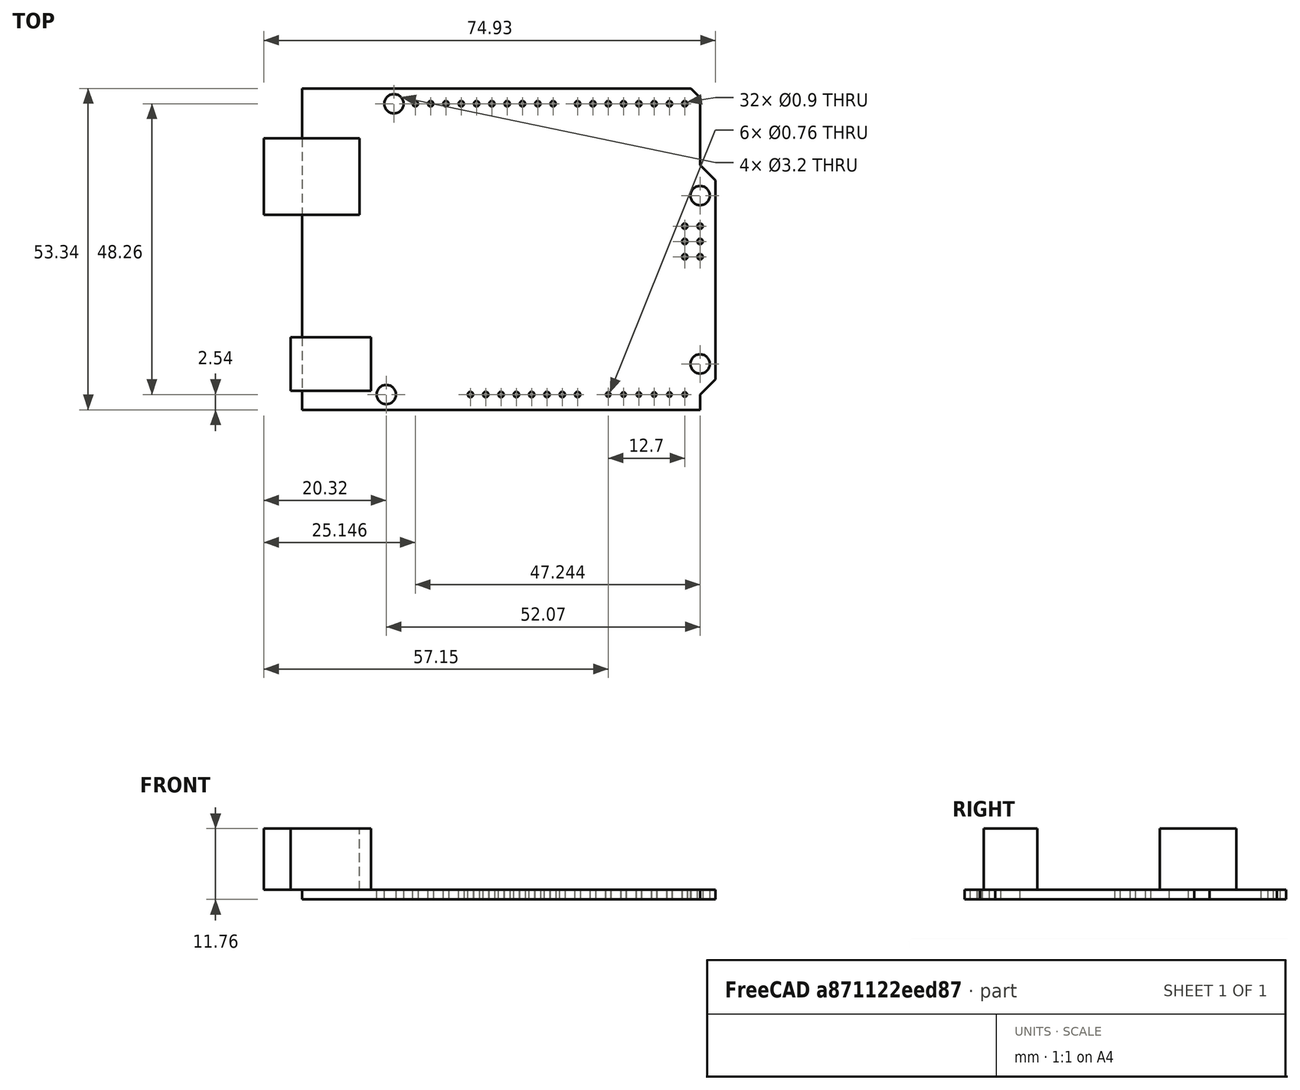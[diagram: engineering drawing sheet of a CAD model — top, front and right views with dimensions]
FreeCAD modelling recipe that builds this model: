
FCSTD DOCUMENT  (FreeCAD 0.21R33694 (Git))
Label: 2405_ARDUNIV
License: All rights reserved
LicenseURL: http://en.wikipedia.org/wiki/All_rights_reserved
objects: TechDraw::DrawViewDimension×40, Sketcher::SketchObject×8, PartDesign::Pocket×6, PartDesign::Pad×2, PartDesign::Body×1, TechDraw::DrawSVGTemplate×1, TechDraw::DrawViewPart×1, TechDraw::DrawPage×1
note: 103 computed .brp shape members not serialized (recipe doc carries the construction recipe); baked Part::Feature solids carry a one-line shape summary decoded from their .brp

FEATURE [Sketcher::SketchObject] Sketch
  FullyConstrained = true
  MapMode = 5
  Support = -> [XY_Plane]
  sketch-geometry (9):
    g0: LineSegment StartX=0 StartY=0 StartZ=0 EndX=66.04 EndY=0 EndZ=0
    g1: LineSegment StartX=66.04 StartY=0 StartZ=0 EndX=66.04 EndY=2.54 EndZ=0
    g2: LineSegment StartX=64.516 StartY=53.34 StartZ=0 EndX=0 EndY=53.34 EndZ=0
    g3: LineSegment StartX=0 StartY=53.34 StartZ=0 EndX=0 EndY=0 EndZ=0
    g4: LineSegment StartX=64.516 StartY=53.34 StartZ=0 EndX=66.04 EndY=51.816 EndZ=0
    g5: LineSegment StartX=66.04 StartY=40.64 StartZ=0 EndX=68.58 EndY=38.1 EndZ=0
    g6: LineSegment StartX=68.58 StartY=38.1 StartZ=0 EndX=68.58 EndY=5.08 EndZ=0
    g7: LineSegment StartX=68.58 StartY=5.08 StartZ=0 EndX=66.04 EndY=2.54 EndZ=0
    g8: LineSegment StartX=66.04 StartY=40.64 StartZ=0 EndX=66.04 EndY=51.816 EndZ=0
  constraints (26):
    c: Coincident(g0,g1)
    c: Coincident(g2,g3)
    c: Coincident(g3,g0)
    c: Horizontal(g0)
    c: Horizontal(g2)
    c: Vertical(g1)
    c: Vertical(g3)
    c: Coincident(g0,g-1)
    c: DistanceY(g3,g3) = 53.34
    c: Coincident(g5,g6)
    c: Vertical(g6)
    c: Coincident(g6,g7)
    c: Coincident(g2,g4)
    c: Coincident(g4,g8)
    c: Coincident(g8,g5)
    c: Coincident(g7,g1)
    c: DistanceY(g1,g1) = 2.54
    c: Distance(g6,g-1) = 5.08
    c: Distance(g6,g1) = 2.54
    c: DistanceX(g2,g2) = 64.516
    c: Distance(g4,g-1) = 51.816
    c: Vertical(g5,g1)
    c: Vertical(g8)
    c: Distance(g5,g-1) = 40.64
    c: Distance(g5,g-1) = 38.1
    c: Distance(g6,g3) = 68.58
FEATURE [PartDesign::Pad] Pad
  Direction = (0,0,1)
  Length = 1.6
  Length2 = 10
  Profile = -> Sketch
  ReferenceAxis = -> Sketch [N_Axis]
  Reversed = true
  Type = 0
FEATURE [Sketcher::SketchObject] Sketch001
  FullyConstrained = true
  MapMode = 5
  Support = -> [XY_Plane]
  sketch-geometry (8):
    g0: LineSegment StartX=-1.905 StartY=12.065 StartZ=0 EndX=11.43 EndY=12.065 EndZ=0
    g1: LineSegment StartX=11.43 StartY=12.065 StartZ=0 EndX=11.43 EndY=3.175 EndZ=0
    g2: LineSegment StartX=11.43 StartY=3.175 StartZ=0 EndX=-1.905 EndY=3.175 EndZ=0
    g3: LineSegment StartX=-1.905 StartY=3.175 StartZ=0 EndX=-1.905 EndY=12.065 EndZ=0
    g4: LineSegment StartX=-6.35 StartY=45.085 StartZ=0 EndX=9.525 EndY=45.085 EndZ=0
    g5: LineSegment StartX=9.525 StartY=45.085 StartZ=0 EndX=9.525 EndY=32.385 EndZ=0
    g6: LineSegment StartX=9.525 StartY=32.385 StartZ=0 EndX=-6.35 EndY=32.385 EndZ=0
    g7: LineSegment StartX=-6.35 StartY=32.385 StartZ=0 EndX=-6.35 EndY=45.085 EndZ=0
  constraints (24):
    c: Coincident(g0,g1)
    c: Coincident(g1,g2)
    c: Coincident(g2,g3)
    c: Coincident(g3,g0)
    c: Horizontal(g0)
    c: Horizontal(g2)
    c: Vertical(g1)
    c: Vertical(g3)
    c: Coincident(g4,g5)
    c: Coincident(g5,g6)
    c: Coincident(g6,g7)
    c: Coincident(g7,g4)
    c: Horizontal(g4)
    c: Horizontal(g6)
    c: Vertical(g5)
    c: Vertical(g7)
    c: Distance(g2,g-2) = 1.905
    c: Distance(g2,g-1) = 3.175
    c: DistanceY(g3,g3) = 8.89
    c: DistanceX(g0,g0) = 13.335
    c: Distance(g4,g-2) = 6.35
    c: Distance(g6,g-1) = 32.385
    c: DistanceY(g7,g7) = 12.7
    c: DistanceX(g4,g4) = 15.875
FEATURE [PartDesign::Pad] Pad001
  BaseFeature = -> Pad
  Direction = (0,0,1)
  Length = 10.16
  Length2 = 10
  Profile = -> Sketch001
  ReferenceAxis = -> Sketch001 [N_Axis]
  Type = 0
FEATURE [Sketcher::SketchObject] Sketch002
  FullyConstrained = true
  MapMode = 5
  Support = -> [XY_Plane]
  sketch-geometry (4):
    g0: Circle CenterX=13.97 CenterY=2.54 CenterZ=0 NormalX=0 NormalY=0 NormalZ=1 AngleXU=0 Radius=1.6
    g1: Circle CenterX=15.24 CenterY=50.8 CenterZ=0 NormalX=0 NormalY=0 NormalZ=1 AngleXU=0 Radius=1.6
    g2: Circle CenterX=66.04 CenterY=35.56 CenterZ=0 NormalX=0 NormalY=0 NormalZ=1 AngleXU=0 Radius=1.6
    g3: Circle CenterX=66.04 CenterY=7.62 CenterZ=0 NormalX=0 NormalY=0 NormalZ=1 AngleXU=0 Radius=1.6
  constraints (12):
    c: Equal(g1,g2)
    c: Equal(g2,g3)
    c: Equal(g3,g0)
    c: Radius(g1) = 1.6
    c: Distance(g0,g-1) = 2.54
    c: Distance(g0,g-2) = 13.97
    c: Distance(g1,g-1) = 50.8
    c: Distance(g1,g-2) = 15.24
    c: Distance(g3,g-1) = 7.62
    c: Distance(g3,g-2) = 66.04
    c: Vertical(g2,g3)
    c: Distance(g2,g-1) = 35.56
FEATURE [PartDesign::Pocket] Pocket
  BaseFeature = -> Pad001
  Direction = (0,0,-1)
  Length = 5.00126
  Length2 = 5
  Profile = -> Sketch002
  ReferenceAxis = -> Sketch002 [N_Axis]
  Type = 0
FEATURE [Sketcher::SketchObject] Sketch003
  FullyConstrained = true
  MapMode = 5
  Support = -> [XY_Plane]
  sketch-geometry (6):
    g0: Circle CenterX=63.5 CenterY=30.48 CenterZ=0 NormalX=0 NormalY=0 NormalZ=1 AngleXU=0 Radius=0.45
    g1: Circle CenterX=63.5 CenterY=27.94 CenterZ=0 NormalX=0 NormalY=0 NormalZ=1 AngleXU=0 Radius=0.45
    g2: Circle CenterX=63.5 CenterY=25.4 CenterZ=0 NormalX=0 NormalY=0 NormalZ=1 AngleXU=0 Radius=0.45
    g3: Circle CenterX=66.04 CenterY=30.48 CenterZ=0 NormalX=0 NormalY=0 NormalZ=1 AngleXU=0 Radius=0.45
    g4: Circle CenterX=66.04 CenterY=27.94 CenterZ=0 NormalX=0 NormalY=0 NormalZ=1 AngleXU=0 Radius=0.45
    g5: Circle CenterX=66.04 CenterY=25.4 CenterZ=0 NormalX=0 NormalY=0 NormalZ=1 AngleXU=0 Radius=0.45
  constraints (18):
    c: Distance(g0,g-2) = 63.5
    c: Distance(g0,g-1) = 30.48
    c: Radius(g0) = 0.45
    c: Equal(g1,g0)
    c: Equal(g0,g3)
    c: Equal(g3,g4)
    c: Equal(g4,g5)
    c: Equal(g5,g2)
    c: Vertical(g0,g1)
    c: Vertical(g1,g2)
    c: Vertical(g3,g4)
    c: Vertical(g4,g5)
    c: Horizontal(g0,g3)
    c: Horizontal(g4,g1)
    c: Horizontal(g5,g2)
    c: Distance(g0,g1) = 2.54
    c: Distance(g1,g2) = 2.54
    c: Distance(g2,g5) = 2.54
FEATURE [PartDesign::Pocket] Pocket001
  BaseFeature = -> Pocket
  Direction = (0,0,-1)
  Length = 5.00126
  Length2 = 5
  Profile = -> Sketch003
  ReferenceAxis = -> Sketch003 [N_Axis]
  Type = 0
FEATURE [Sketcher::SketchObject] Sketch004
  FullyConstrained = true
  MapMode = 5
  Support = -> [XY_Plane]
  sketch-geometry (9):
    g0: Circle CenterX=27.94 CenterY=2.54 CenterZ=0 NormalX=0 NormalY=0 NormalZ=1 AngleXU=0 Radius=0.45
    g1: Circle CenterX=30.48 CenterY=2.54 CenterZ=0 NormalX=0 NormalY=0 NormalZ=1 AngleXU=0 Radius=0.45
    g2: Circle CenterX=33.02 CenterY=2.54 CenterZ=0 NormalX=0 NormalY=0 NormalZ=1 AngleXU=0 Radius=0.45
    g3: Circle CenterX=35.56 CenterY=2.54 CenterZ=0 NormalX=0 NormalY=0 NormalZ=1 AngleXU=0 Radius=0.45
    g4: Circle CenterX=40.64 CenterY=2.54 CenterZ=0 NormalX=0 NormalY=0 NormalZ=1 AngleXU=0 Radius=0.45
    g5: Circle CenterX=43.18 CenterY=2.54 CenterZ=0 NormalX=0 NormalY=0 NormalZ=1 AngleXU=0 Radius=0.45
    g6: Circle CenterX=45.72 CenterY=2.54 CenterZ=0 NormalX=0 NormalY=0 NormalZ=1 AngleXU=0 Radius=0.45
    g7: LineSegment StartX=27.94 StartY=2.54 StartZ=0 EndX=45.72 EndY=2.54 EndZ=0
    g8: Circle CenterX=38.1 CenterY=2.54 CenterZ=0 NormalX=0 NormalY=0 NormalZ=1 AngleXU=0 Radius=0.45
  constraints (26):
    c: Equal(g0,g1)
    c: Equal(g1,g2)
    c: Equal(g2,g3)
    c: Equal(g3,g4)
    c: Equal(g4,g5)
    c: Radius(g0) = 0.45
    c: Distance(g0,g-2) = 27.94
    c: Distance(g0,g-1) = 2.54
    c: Coincident(g7,g0)
    c: Coincident(g7,g6)
    c: Horizontal(g7)
    c: DistanceX(g7,g7) = 17.78
    c: PointOnObject(g1,g7)
    c: PointOnObject(g2,g7)
    c: PointOnObject(g3,g7)
    c: PointOnObject(g4,g7)
    c: PointOnObject(g5,g7)
    c: PointOnObject(g8,g7)
    c: Equal(g8,g0)
    c: Distance(g1,g0) = 2.54
    c: Distance(g2,g1) = 2.54
    c: Distance(g3,g2) = 2.54
    c: Distance(g8,g3) = 2.54
    c: Distance(g4,g8) = 2.54
    c: Distance(g5,g4) = 2.54
    c: Equal(g0,g6)
FEATURE [PartDesign::Pocket] Pocket002
  BaseFeature = -> Pocket001
  Direction = (0,0,-1)
  Length = 5.00126
  Length2 = 5
  Profile = -> Sketch004
  ReferenceAxis = -> Sketch004 [N_Axis]
  Type = 0
FEATURE [Sketcher::SketchObject] Sketch005
  FullyConstrained = true
  MapMode = 5
  Support = -> [XY_Plane]
  sketch-geometry (7):
    g0: LineSegment StartX=50.8 StartY=2.54 StartZ=0 EndX=63.5 EndY=2.54 EndZ=0
    g1: Circle CenterX=50.8 CenterY=2.54 CenterZ=0 NormalX=0 NormalY=0 NormalZ=1 AngleXU=0 Radius=0.381
    g2: Circle CenterX=63.5 CenterY=2.54 CenterZ=0 NormalX=0 NormalY=0 NormalZ=1 AngleXU=0 Radius=0.381
    g3: Circle CenterX=60.96 CenterY=2.54 CenterZ=0 NormalX=0 NormalY=0 NormalZ=1 AngleXU=0 Radius=0.381
    g4: Circle CenterX=58.42 CenterY=2.54 CenterZ=0 NormalX=0 NormalY=0 NormalZ=1 AngleXU=0 Radius=0.381
    g5: Circle CenterX=55.88 CenterY=2.54 CenterZ=0 NormalX=0 NormalY=0 NormalZ=1 AngleXU=0 Radius=0.381
    g6: Circle CenterX=53.34 CenterY=2.54 CenterZ=0 NormalX=0 NormalY=0 NormalZ=1 AngleXU=0 Radius=0.381
  constraints (20):
    c: Horizontal(g0)
    c: Distance(g0,g-1) = 2.54
    c: Distance(g0,g-2) = 50.8
    c: DistanceX(g0,g0) = 12.7
    c: Coincident(g1,g0)
    c: Coincident(g2,g0)
    c: PointOnObject(g3,g0)
    c: PointOnObject(g4,g0)
    c: PointOnObject(g5,g0)
    c: PointOnObject(g6,g0)
    c: Distance(g1,g6) = 2.54
    c: Distance(g5,g6) = 2.54
    c: Distance(g4,g5) = 2.54
    c: Distance(g3,g4) = 2.54
    c: Equal(g1,g6)
    c: Equal(g6,g5)
    c: Equal(g5,g4)
    c: Equal(g4,g3)
    c: Equal(g3,g2)
    c: Radius(g1) = 0.381
FEATURE [PartDesign::Pocket] Pocket003
  BaseFeature = -> Pocket002
  Direction = (0,0,-1)
  Length = 5.00126
  Length2 = 5
  Profile = -> Sketch005
  ReferenceAxis = -> Sketch005 [N_Axis]
  Type = 0
FEATURE [Sketcher::SketchObject] Sketch006
  FullyConstrained = true
  MapMode = 5
  Support = -> [XY_Plane]
  sketch-geometry (9):
    g0: LineSegment StartX=45.72 StartY=50.8 StartZ=0 EndX=63.5 EndY=50.8 EndZ=0
    g1: Circle CenterX=45.72 CenterY=50.8 CenterZ=0 NormalX=0 NormalY=0 NormalZ=1 AngleXU=0 Radius=0.45
    g2: Circle CenterX=63.5 CenterY=50.8 CenterZ=0 NormalX=0 NormalY=0 NormalZ=1 AngleXU=0 Radius=0.45
    g3: Circle CenterX=48.26 CenterY=50.8 CenterZ=0 NormalX=0 NormalY=0 NormalZ=1 AngleXU=0 Radius=0.45
    g4: Circle CenterX=50.8 CenterY=50.8 CenterZ=0 NormalX=0 NormalY=0 NormalZ=1 AngleXU=0 Radius=0.45
    g5: Circle CenterX=53.34 CenterY=50.8 CenterZ=0 NormalX=0 NormalY=0 NormalZ=1 AngleXU=0 Radius=0.45
    g6: Circle CenterX=55.88 CenterY=50.8 CenterZ=0 NormalX=0 NormalY=0 NormalZ=1 AngleXU=0 Radius=0.45
    g7: Circle CenterX=58.42 CenterY=50.8 CenterZ=0 NormalX=0 NormalY=0 NormalZ=1 AngleXU=0 Radius=0.45
    g8: Circle CenterX=60.96 CenterY=50.8 CenterZ=0 NormalX=0 NormalY=0 NormalZ=1 AngleXU=0 Radius=0.45
  constraints (26):
    c: Horizontal(g0)
    c: Distance(g0,g-2) = 45.72
    c: DistanceX(g0,g0) = 17.78
    c: Coincident(g1,g0)
    c: Coincident(g2,g0)
    c: PointOnObject(g3,g0)
    c: PointOnObject(g4,g0)
    c: PointOnObject(g5,g0)
    c: PointOnObject(g6,g0)
    c: PointOnObject(g7,g0)
    c: PointOnObject(g8,g0)
    c: Distance(g3,g1) = 2.54
    c: Distance(g4,g3) = 2.54
    c: Distance(g5,g4) = 2.54
    c: Distance(g6,g5) = 2.54
    c: Distance(g7,g6) = 2.54
    c: Distance(g8,g7) = 2.54
    c: Equal(g1,g3)
    c: Equal(g3,g4)
    c: Equal(g4,g5)
    c: Equal(g5,g6)
    c: Equal(g6,g7)
    c: Equal(g8,g7)
    c: Equal(g2,g8)
    c: Radius(g1) = 0.45
    c: Distance(g1,g-1) = 50.8
FEATURE [PartDesign::Pocket] Pocket004
  BaseFeature = -> Pocket003
  Direction = (0,0,-1)
  Length = 5.00126
  Length2 = 5
  Profile = -> Sketch006
  ReferenceAxis = -> Sketch006 [N_Axis]
  Type = 0
FEATURE [Sketcher::SketchObject] Sketch007
  FullyConstrained = true
  MapMode = 5
  Support = -> [XY_Plane]
  sketch-geometry (11):
    g0: LineSegment StartX=18.796 StartY=50.8 StartZ=0 EndX=41.656 EndY=50.8 EndZ=0
    g1: Circle CenterX=18.796 CenterY=50.8 CenterZ=0 NormalX=0 NormalY=0 NormalZ=1 AngleXU=0 Radius=0.45
    g2: Circle CenterX=41.656 CenterY=50.8 CenterZ=0 NormalX=0 NormalY=0 NormalZ=1 AngleXU=0 Radius=0.45
    g3: Circle CenterX=21.336 CenterY=50.8 CenterZ=0 NormalX=0 NormalY=0 NormalZ=1 AngleXU=0 Radius=0.45
    g4: Circle CenterX=23.876 CenterY=50.8 CenterZ=0 NormalX=0 NormalY=0 NormalZ=1 AngleXU=0 Radius=0.45
    g5: Circle CenterX=26.416 CenterY=50.8 CenterZ=0 NormalX=0 NormalY=0 NormalZ=1 AngleXU=0 Radius=0.45
    g6: Circle CenterX=31.496 CenterY=50.8 CenterZ=0 NormalX=0 NormalY=0 NormalZ=1 AngleXU=0 Radius=0.45
    g7: Circle CenterX=34.036 CenterY=50.8 CenterZ=0 NormalX=0 NormalY=0 NormalZ=1 AngleXU=0 Radius=0.45
    g8: Circle CenterX=36.576 CenterY=50.8 CenterZ=0 NormalX=0 NormalY=0 NormalZ=1 AngleXU=0 Radius=0.45
    g9: Circle CenterX=39.116 CenterY=50.8 CenterZ=0 NormalX=0 NormalY=0 NormalZ=1 AngleXU=0 Radius=0.45
    g10: Circle CenterX=28.956 CenterY=50.8 CenterZ=0 NormalX=0 NormalY=0 NormalZ=1 AngleXU=0 Radius=0.45
  constraints (32):
    c: Horizontal(g0)
    c: Distance(g0,g-1) = 50.8
    c: Distance(g0,g-2) = 18.796
    c: DistanceX(g0,g0) = 22.86
    c: Coincident(g1,g0)
    c: Coincident(g2,g0)
    c: PointOnObject(g3,g0)
    c: PointOnObject(g4,g0)
    c: PointOnObject(g5,g0)
    c: PointOnObject(g6,g0)
    c: PointOnObject(g7,g0)
    c: PointOnObject(g8,g0)
    c: PointOnObject(g9,g0)
    c: Distance(g3,g1) = 2.54
    c: Distance(g4,g3) = 2.54
    c: Distance(g5,g4) = 2.54
    c: PointOnObject(g10,g0)
    c: Distance(g10,g5) = 2.54
    c: Distance(g6,g10) = 2.54
    c: Distance(g7,g6) = 2.54
    c: Distance(g8,g7) = 2.54
    c: Distance(g9,g8) = 2.54
    c: Equal(g1,g3)
    c: Equal(g3,g4)
    c: Equal(g4,g5)
    c: Equal(g5,g10)
    c: Equal(g6,g10)
    c: Equal(g7,g6)
    c: Equal(g8,g7)
    c: Equal(g9,g8)
    c: Equal(g2,g9)
    c: Radius(g1) = 0.45
FEATURE [PartDesign::Pocket] Pocket005
  BaseFeature = -> Pocket004
  Direction = (0,0,-1)
  Length = 5.00126
  Length2 = 5
  Profile = -> Sketch007
  ReferenceAxis = -> Sketch007 [N_Axis]
  Type = 0
FEATURE [PartDesign::Body] Body
  Group = -> [Sketch,Pad,Sketch001,Pad001,Sketch002,Pocket,Sketch003,Pocket001,Sketch004,Pocket002,Sketch005,Pocket003,Sketch006,Pocket004,Sketch007,Pocket005]
  Origin = -> Origin
  Tip = -> Pocket005
FEATURE [TechDraw::DrawSVGTemplate] Template
  EditableTexts = AUTHOR_NAME=K.Sato; DN=2405; DRAWING_TITLE=BASEBOARD; FC-DATE=2024/03/28; FC-REV=REV A1; FC-SC=mm x2; FC-SH=1 / 1; FC-SI=A4; FreeCAD_DRAWING=ARDUINO UNO R3 BOARD DIMENSION; PN=1
  Height = 210
  Orientation = 1
  Template = /Applications/FreeCAD.app/Contents/Resources/share/Mod/TechDraw/Templates/A4_Landscape_ISO7200TD.svg
  Width = 297
FEATURE [TechDraw::DrawViewPart] View
  CoarseView = false
  Direction = (0,0,1)
  Focus = 100
  HardHidden = false
  IsoCount = 0
  IsoHidden = false
  IsoVisible = false
  LockPosition = true
  Perspective = false
  Rotation = 0
  Scale = 2
  ScaleType = 1
  ScrubCount = 0
  SeamHidden = false
  SeamVisible = true
  SmoothHidden = false
  SmoothVisible = true
  Source = -> [Pocket005]
  X = 145.331
  XDirection = (1,0,0)
  Y = 119.238
FEATURE [TechDraw::DrawViewDimension] Dimension
  AngleOverride = false
  Arbitrary = false
  ArbitraryTolerances = false
  EqualTolerance = true
  ExtensionAngle = 0
  FormatSpec = %.2w
  FormatSpecOverTolerance = %+.2w
  FormatSpecUnderTolerance = %+.2w
  Inverted = false
  LineAngle = 0
  LockPosition = false
  MeasureType = 1
  OverTolerance = 0
  References2D = -> [View]
  Rotation = 0
  ScaleType = 0
  TheoreticalExact = false
  Type = 1
  UnderTolerance = 0
  X = 8.48278
  Y = -57.3383
FEATURE [TechDraw::DrawViewDimension] Dimension001
  AngleOverride = false
  Arbitrary = false
  ArbitraryTolerances = false
  EqualTolerance = true
  ExtensionAngle = 0
  FormatSpec = %.2w
  FormatSpecOverTolerance = %+.2w
  FormatSpecUnderTolerance = %+.2w
  Inverted = false
  LineAngle = 0
  LockPosition = false
  MeasureType = 1
  OverTolerance = 0
  References2D = -> [View]
  Rotation = 0
  ScaleType = 0
  TheoreticalExact = false
  Type = 2
  UnderTolerance = 0
  X = -90.2326
  Y = 0.834304
FEATURE [TechDraw::DrawViewDimension] Dimension002
  AngleOverride = false
  Arbitrary = false
  ArbitraryTolerances = false
  EqualTolerance = true
  ExtensionAngle = 0
  FormatSpec = %.2w
  FormatSpecOverTolerance = %+.2w
  FormatSpecUnderTolerance = %+.2w
  Inverted = false
  LineAngle = 0
  LockPosition = false
  MeasureType = 1
  OverTolerance = 0
  References2D = -> [View]
  Rotation = 0
  ScaleType = 0
  TheoreticalExact = false
  Type = 2
  UnderTolerance = 0
  X = -58.3312
  Y = -34.7674
FEATURE [TechDraw::DrawViewDimension] Dimension003
  AngleOverride = false
  Arbitrary = false
  ArbitraryTolerances = false
  EqualTolerance = true
  ExtensionAngle = 0
  FormatSpec = %.2w
  FormatSpecOverTolerance = %+.2w
  FormatSpecUnderTolerance = %+.2w
  Inverted = false
  LineAngle = 0
  LockPosition = false
  MeasureType = 1
  OverTolerance = 0
  References2D = -> [View]
  Rotation = 0
  ScaleType = 0
  TheoreticalExact = false
  Type = 1
  UnderTolerance = 0
  X = -48.8176
  Y = -37.0251
FEATURE [TechDraw::DrawViewDimension] Dimension004
  AngleOverride = false
  Arbitrary = false
  ArbitraryTolerances = false
  EqualTolerance = true
  ExtensionAngle = 0
  FormatSpec = %.2w
  FormatSpecOverTolerance = %+.2w
  FormatSpecUnderTolerance = %+.2w
  Inverted = false
  LineAngle = 0
  LockPosition = false
  MeasureType = 1
  OverTolerance = 0
  References2D = -> [View]
  Rotation = 0
  ScaleType = 0
  TheoreticalExact = false
  Type = 0
  UnderTolerance = 0
  X = -69.0599
  Y = 24.0524
FEATURE [TechDraw::DrawViewDimension] Dimension005
  AngleOverride = false
  Arbitrary = false
  ArbitraryTolerances = false
  EqualTolerance = true
  ExtensionAngle = 0
  FormatSpec = %.2w
  FormatSpecOverTolerance = %+.2w
  FormatSpecUnderTolerance = %+.2w
  Inverted = false
  LineAngle = 0
  LockPosition = false
  MeasureType = 1
  OverTolerance = 0
  References2D = -> [View]
  Rotation = 0
  ScaleType = 0
  TheoreticalExact = false
  Type = 1
  UnderTolerance = 0
  X = -54.3922
  Y = 21.3894
FEATURE [TechDraw::DrawViewDimension] Dimension006
  AngleOverride = false
  Arbitrary = false
  ArbitraryTolerances = false
  EqualTolerance = true
  ExtensionAngle = 0
  FormatSpec = %.2w
  FormatSpecOverTolerance = %+.2w
  FormatSpecUnderTolerance = %+.2w
  Inverted = false
  LineAngle = 0
  LockPosition = false
  MeasureType = 1
  OverTolerance = 0
  References2D = -> [View]
  Rotation = 0
  ScaleType = 0
  TheoreticalExact = false
  Type = 2
  UnderTolerance = 0
  X = -73.3308
  Y = -48.1712
FEATURE [TechDraw::DrawViewDimension] Dimension008
  AngleOverride = false
  Arbitrary = false
  ArbitraryTolerances = false
  EqualTolerance = true
  ExtensionAngle = 0
  FormatSpec = %.2w
  FormatSpecOverTolerance = %+.2w
  FormatSpecUnderTolerance = %+.2w
  Inverted = false
  LineAngle = 0
  LockPosition = false
  MeasureType = 1
  OverTolerance = 0
  References2D = -> [View]
  Rotation = 0
  ScaleType = 0
  TheoreticalExact = false
  Type = 1
  UnderTolerance = 0
  X = -72.4898
  Y = -17.8173
FEATURE [TechDraw::DrawViewDimension] Dimension009
  AngleOverride = false
  Arbitrary = false
  ArbitraryTolerances = false
  EqualTolerance = true
  ExtensionAngle = 0
  FormatSpec = %.2w
  FormatSpecOverTolerance = %+.2w
  FormatSpecUnderTolerance = %+.2w
  Inverted = false
  LineAngle = 0
  LockPosition = false
  MeasureType = 1
  OverTolerance = 0
  References2D = -> [View]
  Rotation = 0
  ScaleType = 0
  TheoreticalExact = false
  Type = 2
  UnderTolerance = 0
  X = -81.0782
  Y = -19.8727
FEATURE [TechDraw::DrawViewDimension] Dimension010
  AngleOverride = false
  Arbitrary = false
  ArbitraryTolerances = false
  EqualTolerance = true
  ExtensionAngle = 0
  FormatSpec = %.2w
  FormatSpecOverTolerance = %+.2w
  FormatSpecUnderTolerance = %+.2w
  Inverted = false
  LineAngle = 0
  LockPosition = false
  MeasureType = 1
  OverTolerance = 0
  References2D = -> [View]
  Rotation = 0
  ScaleType = 0
  TheoreticalExact = false
  Type = 1
  UnderTolerance = 0
  X = -68.7465
  Y = 10.5994
FEATURE [TechDraw::DrawViewDimension] Dimension011
  AngleOverride = false
  Arbitrary = false
  ArbitraryTolerances = false
  EqualTolerance = true
  ExtensionAngle = 0
  FormatSpec = %.2w
  FormatSpecOverTolerance = %+.2w
  FormatSpecUnderTolerance = %+.2w
  Inverted = false
  LineAngle = 0
  LockPosition = false
  MeasureType = 1
  OverTolerance = 0
  References2D = -> [View]
  Rotation = 0
  ScaleType = 0
  TheoreticalExact = false
  Type = 1
  UnderTolerance = 0
  X = -46.7403
  Y = 48.2214
FEATURE [TechDraw::DrawViewDimension] Dimension013
  AngleOverride = false
  Arbitrary = false
  ArbitraryTolerances = false
  EqualTolerance = true
  ExtensionAngle = 0
  FormatSpec = %.2w
  FormatSpecOverTolerance = %+.2w
  FormatSpecUnderTolerance = %+.2w
  Inverted = false
  LineAngle = 0
  LockPosition = false
  MeasureType = 1
  OverTolerance = 0
  References2D = -> [View]
  Rotation = 0
  ScaleType = 0
  TheoreticalExact = false
  Type = 1
  UnderTolerance = 0
  X = -42.7681
  Y = 64.8716
FEATURE [TechDraw::DrawViewDimension] Dimension014
  AngleOverride = false
  Arbitrary = false
  ArbitraryTolerances = false
  EqualTolerance = true
  ExtensionAngle = 0
  FormatSpec = %.2w
  FormatSpecOverTolerance = %+.2w
  FormatSpecUnderTolerance = %+.2w
  Inverted = false
  LineAngle = 0
  LockPosition = false
  MeasureType = 1
  OverTolerance = 0
  References2D = -> [View]
  Rotation = 0
  ScaleType = 0
  TheoreticalExact = false
  Type = 1
  UnderTolerance = 0
  X = -1.20494
  Y = 64.8287
FEATURE [TechDraw::DrawViewDimension] Dimension016
  AngleOverride = false
  Arbitrary = false
  ArbitraryTolerances = false
  EqualTolerance = true
  ExtensionAngle = 0
  FormatSpec = %.2w
  FormatSpecOverTolerance = %+.2w
  FormatSpecUnderTolerance = %+.2w
  Inverted = false
  LineAngle = 0
  LockPosition = false
  MeasureType = 1
  OverTolerance = 0
  References2D = -> [View]
  Rotation = 0
  ScaleType = 0
  TheoreticalExact = false
  Type = 1
  UnderTolerance = 0
  X = 47.5217
  Y = 64.8407
FEATURE [TechDraw::DrawViewDimension] Dimension018
  AngleOverride = false
  Arbitrary = false
  ArbitraryTolerances = false
  EqualTolerance = true
  ExtensionAngle = 0
  FormatSpec = %.2w
  FormatSpecOverTolerance = %+.2w
  FormatSpecUnderTolerance = %+.2w
  Inverted = false
  LineAngle = 0
  LockPosition = false
  MeasureType = 1
  OverTolerance = 0
  References2D = -> [View]
  Rotation = 0
  ScaleType = 0
  TheoreticalExact = false
  Type = 1
  UnderTolerance = 0
  X = 74.0547
  Y = 37.4933
FEATURE [TechDraw::DrawViewDimension] Dimension019
  AngleOverride = false
  Arbitrary = false
  ArbitraryTolerances = false
  EqualTolerance = true
  ExtensionAngle = 0
  FormatSpec = %.2w
  FormatSpecOverTolerance = %+.2w
  FormatSpecUnderTolerance = %+.2w
  Inverted = false
  LineAngle = 0
  LockPosition = false
  MeasureType = 1
  OverTolerance = 0
  References2D = -> [View]
  Rotation = 0
  ScaleType = 0
  TheoreticalExact = false
  Type = 2
  UnderTolerance = 0
  X = 82.8275
  Y = 19.4049
FEATURE [TechDraw::DrawViewDimension] Dimension020
  AngleOverride = false
  Arbitrary = false
  ArbitraryTolerances = false
  EqualTolerance = true
  ExtensionAngle = 0
  FormatSpec = %.2w
  FormatSpecOverTolerance = %+.2w
  FormatSpecUnderTolerance = %+.2w
  Inverted = false
  LineAngle = 0
  LockPosition = false
  MeasureType = 1
  OverTolerance = 0
  References2D = -> [View]
  Rotation = 0
  ScaleType = 0
  TheoreticalExact = false
  Type = 1
  UnderTolerance = 0
  X = 75.7341
  Y = 61.057
FEATURE [TechDraw::DrawViewDimension] Dimension021
  AngleOverride = false
  Arbitrary = false
  ArbitraryTolerances = false
  EqualTolerance = true
  ExtensionAngle = 0
  FormatSpec = %.2w
  FormatSpecOverTolerance = %+.2w
  FormatSpecUnderTolerance = %+.2w
  Inverted = false
  LineAngle = 0
  LockPosition = false
  MeasureType = 1
  OverTolerance = 0
  References2D = -> [View]
  Rotation = 0
  ScaleType = 0
  TheoreticalExact = false
  Type = 2
  UnderTolerance = 0
  X = 83.3918
  Y = 59.1426
FEATURE [TechDraw::DrawViewDimension] Dimension022
  AngleOverride = false
  Arbitrary = false
  ArbitraryTolerances = false
  EqualTolerance = true
  ExtensionAngle = 0
  FormatSpec = %.2w
  FormatSpecOverTolerance = %+.2w
  FormatSpecUnderTolerance = %+.2w
  Inverted = false
  LineAngle = 0
  LockPosition = false
  MeasureType = 1
  OverTolerance = 0
  References2D = -> [View]
  Rotation = 0
  ScaleType = 0
  TheoreticalExact = false
  Type = 2
  UnderTolerance = 0
  X = 83.3343
  Y = 39.7836
FEATURE [TechDraw::DrawViewDimension] Dimension023
  AngleOverride = false
  Arbitrary = false
  ArbitraryTolerances = false
  EqualTolerance = true
  ExtensionAngle = 0
  FormatSpec = %.2w
  FormatSpecOverTolerance = %+.2w
  FormatSpecUnderTolerance = %+.2w
  Inverted = false
  LineAngle = 0
  LockPosition = false
  MeasureType = 1
  OverTolerance = 0
  References2D = -> [View]
  Rotation = 0
  ScaleType = 0
  TheoreticalExact = false
  Type = 1
  UnderTolerance = 0
  X = -47.3444
  Y = -17.8365
FEATURE [TechDraw::DrawViewDimension] Dimension024
  AngleOverride = false
  Arbitrary = false
  ArbitraryTolerances = false
  EqualTolerance = true
  ExtensionAngle = 0
  FormatSpec = %.2w
  FormatSpecOverTolerance = %+.2w
  FormatSpecUnderTolerance = %+.2w
  Inverted = false
  LineAngle = 0
  LockPosition = false
  MeasureType = 1
  OverTolerance = 0
  References2D = -> [View]
  Rotation = 0
  ScaleType = 0
  TheoreticalExact = false
  Type = 1
  UnderTolerance = 0
  X = -16.9262
  Y = 43.9763
FEATURE [TechDraw::DrawViewDimension] Dimension025
  AngleOverride = false
  Arbitrary = false
  ArbitraryTolerances = false
  EqualTolerance = true
  ExtensionAngle = 0
  FormatSpec = %.2w
  FormatSpecOverTolerance = %+.2w
  FormatSpecUnderTolerance = %+.2w
  Inverted = false
  LineAngle = 0
  LockPosition = false
  MeasureType = 1
  OverTolerance = 0
  References2D = -> [View]
  Rotation = 0
  ScaleType = 0
  TheoreticalExact = false
  Type = 2
  UnderTolerance = 0
  X = -29.5784
  Y = -34.4168
FEATURE [TechDraw::DrawViewDimension] Dimension026
  AngleOverride = false
  Arbitrary = false
  ArbitraryTolerances = false
  EqualTolerance = true
  ExtensionAngle = 0
  FormatSpec = ⌀%.2w
  FormatSpecOverTolerance = %+.2w
  FormatSpecUnderTolerance = %+.2w
  Inverted = false
  LineAngle = 0
  LockPosition = false
  MeasureType = 1
  OverTolerance = 0
  References2D = -> [View]
  Rotation = 0
  ScaleType = 0
  TheoreticalExact = false
  Type = 5
  UnderTolerance = 0
  X = -21.1247
  Y = -31.6132
FEATURE [TechDraw::DrawViewDimension] Dimension027
  AngleOverride = false
  Arbitrary = false
  ArbitraryTolerances = false
  EqualTolerance = true
  ExtensionAngle = 0
  FormatSpec = %.2w
  FormatSpecOverTolerance = %+.2w
  FormatSpecUnderTolerance = %+.2w
  Inverted = false
  LineAngle = 0
  LockPosition = false
  MeasureType = 1
  OverTolerance = 0
  References2D = -> [View]
  Rotation = 0
  ScaleType = 0
  TheoreticalExact = false
  Type = 1
  UnderTolerance = 0
  X = -34.7894
  Y = -12.9256
FEATURE [TechDraw::DrawViewDimension] Dimension028
  AngleOverride = false
  Arbitrary = false
  ArbitraryTolerances = false
  EqualTolerance = true
  ExtensionAngle = 0
  FormatSpec = %.2w
  FormatSpecOverTolerance = %+.2w
  FormatSpecUnderTolerance = %+.2w
  Inverted = false
  LineAngle = 0
  LockPosition = false
  MeasureType = 1
  OverTolerance = 0
  References2D = -> [View]
  Rotation = 0
  ScaleType = 0
  TheoreticalExact = false
  Type = 1
  UnderTolerance = 0
  X = -14.0936
  Y = -8.18108
FEATURE [TechDraw::DrawViewDimension] Dimension029
  AngleOverride = false
  Arbitrary = false
  ArbitraryTolerances = false
  EqualTolerance = true
  ExtensionAngle = 0
  FormatSpec = %.2w
  FormatSpecOverTolerance = %+.2w
  FormatSpecUnderTolerance = %+.2w
  Inverted = false
  LineAngle = 0
  LockPosition = false
  MeasureType = 1
  OverTolerance = 0
  References2D = -> [View]
  Rotation = 0
  ScaleType = 0
  TheoreticalExact = false
  Type = 1
  UnderTolerance = 0
  X = 0.480533
  Y = 28.2748
FEATURE [TechDraw::DrawViewDimension] Dimension030
  AngleOverride = false
  Arbitrary = false
  ArbitraryTolerances = false
  EqualTolerance = true
  ExtensionAngle = 0
  FormatSpec = %.2w
  FormatSpecOverTolerance = %+.2w
  FormatSpecUnderTolerance = %+.2w
  Inverted = false
  LineAngle = 0
  LockPosition = false
  MeasureType = 1
  OverTolerance = 0
  References2D = -> [View]
  Rotation = 0
  ScaleType = 0
  TheoreticalExact = false
  Type = 1
  UnderTolerance = 0
  X = 24.8466
  Y = 64.8407
FEATURE [TechDraw::DrawViewDimension] Dimension031
  AngleOverride = false
  Arbitrary = false
  ArbitraryTolerances = false
  EqualTolerance = true
  ExtensionAngle = 0
  FormatSpec = %.2w
  FormatSpecOverTolerance = %+.2w
  FormatSpecUnderTolerance = %+.2w
  Inverted = false
  LineAngle = 0
  LockPosition = false
  MeasureType = 1
  OverTolerance = 0
  References2D = -> [View]
  Rotation = 0
  ScaleType = 0
  TheoreticalExact = false
  Type = 1
  UnderTolerance = 0
  X = 32.875
  Y = -38.1034
FEATURE [TechDraw::DrawViewDimension] Dimension032
  AngleOverride = false
  Arbitrary = false
  ArbitraryTolerances = false
  EqualTolerance = true
  ExtensionAngle = 0
  FormatSpec = %.2w
  FormatSpecOverTolerance = %+.2w
  FormatSpecUnderTolerance = %+.2w
  Inverted = false
  LineAngle = 0
  LockPosition = false
  MeasureType = 1
  OverTolerance = 0
  References2D = -> [View]
  Rotation = 0
  ScaleType = 0
  TheoreticalExact = false
  Type = 1
  UnderTolerance = 0
  X = 12.2624
  Y = -38.1866
FEATURE [TechDraw::DrawViewDimension] Dimension033
  AngleOverride = false
  Arbitrary = false
  ArbitraryTolerances = false
  EqualTolerance = true
  ExtensionAngle = 0
  FormatSpec = %.2w
  FormatSpecOverTolerance = %+.2w
  FormatSpecUnderTolerance = %+.2w
  Inverted = false
  LineAngle = 0
  LockPosition = false
  MeasureType = 1
  OverTolerance = 0
  References2D = -> [View]
  Rotation = 0
  ScaleType = 0
  TheoreticalExact = false
  Type = 1
  UnderTolerance = 0
  X = 51.8203
  Y = -38.1034
FEATURE [TechDraw::DrawViewDimension] Dimension034
  AngleOverride = false
  Arbitrary = false
  ArbitraryTolerances = false
  EqualTolerance = true
  ExtensionAngle = 0
  FormatSpec = %.2w
  FormatSpecOverTolerance = %+.2w
  FormatSpecUnderTolerance = %+.2w
  Inverted = false
  LineAngle = 0
  LockPosition = false
  MeasureType = 1
  OverTolerance = 0
  References2D = -> [View]
  Rotation = 0
  ScaleType = 0
  TheoreticalExact = false
  Type = 2
  UnderTolerance = 0
  X = 78.6731
  Y = -60.8699
FEATURE [TechDraw::DrawViewDimension] Dimension035
  AngleOverride = false
  Arbitrary = false
  ArbitraryTolerances = false
  EqualTolerance = true
  ExtensionAngle = 0
  FormatSpec = %.2w
  FormatSpecOverTolerance = %+.2w
  FormatSpecUnderTolerance = %+.2w
  Inverted = false
  LineAngle = 0
  LockPosition = false
  MeasureType = 1
  OverTolerance = 0
  References2D = -> [View]
  Rotation = 0
  ScaleType = 0
  TheoreticalExact = false
  Type = 2
  UnderTolerance = 0
  X = 81.546
  Y = -30.909
FEATURE [TechDraw::DrawViewDimension] Dimension036
  AngleOverride = false
  Arbitrary = false
  ArbitraryTolerances = false
  EqualTolerance = true
  ExtensionAngle = 0
  FormatSpec = %.2w
  FormatSpecOverTolerance = %+.2w
  FormatSpecUnderTolerance = %+.2w
  Inverted = false
  LineAngle = 0
  LockPosition = false
  MeasureType = 1
  OverTolerance = 0
  References2D = -> [View]
  Rotation = 0
  ScaleType = 0
  TheoreticalExact = false
  Type = 1
  UnderTolerance = 0
  X = 64.1496
  Y = -54.0419
FEATURE [TechDraw::DrawViewDimension] Dimension037
  AngleOverride = false
  Arbitrary = false
  ArbitraryTolerances = false
  EqualTolerance = true
  ExtensionAngle = 0
  FormatSpec = %.2w
  FormatSpecOverTolerance = %+.2w
  FormatSpecUnderTolerance = %+.2w
  Inverted = false
  LineAngle = 0
  LockPosition = false
  MeasureType = 1
  OverTolerance = 0
  References2D = -> [View]
  Rotation = 0
  ScaleType = 0
  TheoreticalExact = false
  Type = 2
  UnderTolerance = 0
  X = 85.0991
  Y = -20.7932
FEATURE [TechDraw::DrawViewDimension] Dimension038
  AngleOverride = false
  Arbitrary = false
  ArbitraryTolerances = false
  EqualTolerance = true
  ExtensionAngle = 0
  FormatSpec = %.2w
  FormatSpecOverTolerance = %+.2w
  FormatSpecUnderTolerance = %+.2w
  Inverted = false
  LineAngle = 0
  LockPosition = false
  MeasureType = 1
  OverTolerance = 0
  References2D = -> [View]
  Rotation = 0
  ScaleType = 0
  TheoreticalExact = false
  Type = 2
  UnderTolerance = 0
  X = 44.6961
  Y = -8.92288
FEATURE [TechDraw::DrawViewDimension] Dimension039
  AngleOverride = false
  Arbitrary = false
  ArbitraryTolerances = false
  EqualTolerance = true
  ExtensionAngle = 0
  FormatSpec = %.2w
  FormatSpecOverTolerance = %+.2w
  FormatSpecUnderTolerance = %+.2w
  Inverted = false
  LineAngle = 0
  LockPosition = false
  MeasureType = 1
  OverTolerance = 0
  References2D = -> [View]
  Rotation = 0
  ScaleType = 0
  TheoreticalExact = false
  Type = 2
  UnderTolerance = 0
  X = 88.9522
  Y = -10.9013
FEATURE [TechDraw::DrawViewDimension] Dimension040
  AngleOverride = false
  Arbitrary = false
  ArbitraryTolerances = false
  EqualTolerance = true
  ExtensionAngle = 0
  FormatSpec = %.2w
  FormatSpecOverTolerance = %+.2w
  FormatSpecUnderTolerance = %+.2w
  Inverted = false
  LineAngle = 0
  LockPosition = false
  MeasureType = 1
  OverTolerance = 0
  References2D = -> [View]
  Rotation = 0
  ScaleType = 0
  TheoreticalExact = false
  Type = 1
  UnderTolerance = 0
  X = 60.0862
  Y = 16.0101
FEATURE [TechDraw::DrawViewDimension] Dimension042
  AngleOverride = false
  Arbitrary = false
  ArbitraryTolerances = false
  EqualTolerance = true
  ExtensionAngle = 0
  FormatSpec = %.2w
  FormatSpecOverTolerance = %+.2w
  FormatSpecUnderTolerance = %+.2w
  Inverted = false
  LineAngle = 0
  LockPosition = false
  MeasureType = 1
  OverTolerance = 0
  References2D = -> [View]
  Rotation = 0
  ScaleType = 0
  TheoreticalExact = false
  Type = 2
  UnderTolerance = 0
  X = -29.2462
  Y = 35.7304
FEATURE [TechDraw::DrawViewDimension] Dimension043
  AngleOverride = false
  Arbitrary = false
  ArbitraryTolerances = false
  EqualTolerance = true
  ExtensionAngle = 0
  FormatSpec = %.2w
  FormatSpecOverTolerance = %+.2w
  FormatSpecUnderTolerance = %+.2w
  Inverted = false
  LineAngle = 0
  LockPosition = false
  MeasureType = 1
  OverTolerance = 0
  References2D = -> [View]
  Rotation = 0
  ScaleType = 0
  TheoreticalExact = false
  Type = 1
  UnderTolerance = 0
  X = 50.079
  Y = 45.7097
FEATURE [TechDraw::DrawViewDimension] Dimension044
  AngleOverride = false
  Arbitrary = false
  ArbitraryTolerances = false
  EqualTolerance = true
  ExtensionAngle = 0
  FormatSpec = ⌀%.2w
  FormatSpecOverTolerance = %+.2w
  FormatSpecUnderTolerance = %+.2w
  Inverted = false
  LineAngle = 0
  LockPosition = false
  MeasureType = 1
  OverTolerance = 0
  References2D = -> [View]
  Rotation = 0
  ScaleType = 0
  TheoreticalExact = false
  Type = 5
  UnderTolerance = 0
  X = 51.4761
  Y = 35.8639
FEATURE [TechDraw::DrawPage] Page
  KeepUpdated = true
  NextBalloonIndex = 1
  ProjectionType = 0
  Template = -> Template
  Views = -> [View,Dimension,Dimension001,Dimension002,Dimension003,Dimension004,Dimension005,Dimension006,Dimension008,Dimension009,Dimension010,Dimension011,Dimension013,Dimension014,Dimension016,Dimension018,Dimension019,Dimension020,Dimension021,Dimension022,Dimension023,Dimension024,Dimension025,Dimension026,Dimension027,Dimension028,Dimension029,Dimension030,Dimension031,Dimension032,Dimension033,+10 more]
